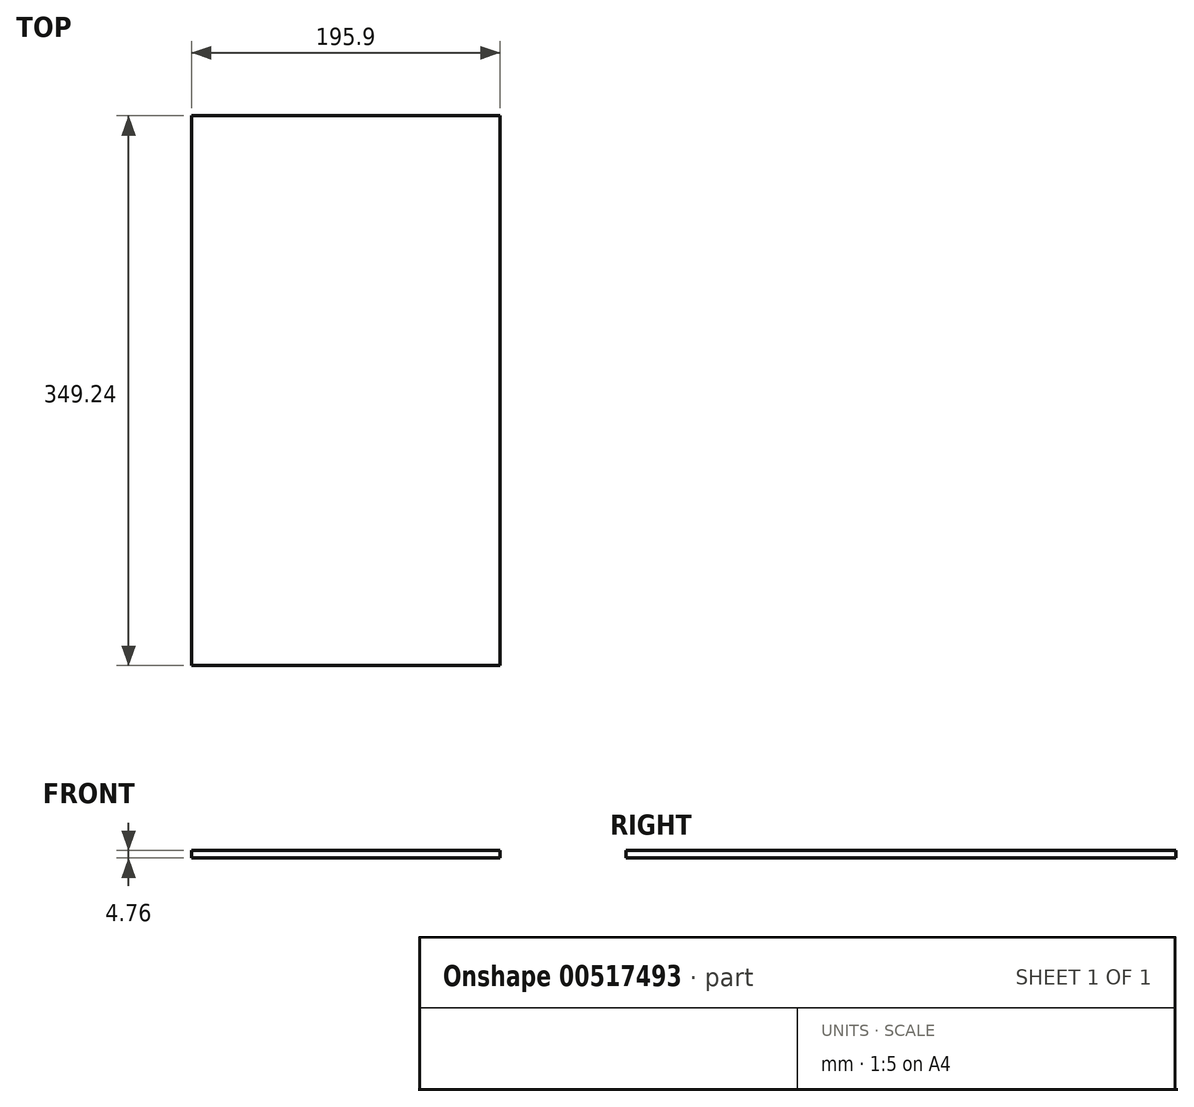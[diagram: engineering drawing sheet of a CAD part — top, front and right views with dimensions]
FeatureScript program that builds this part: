
annotation { "Feature Type Name" : "Feature", "Feature Type Description" : "" }
export const myFeature = defineFeature(function(context is Context, id is Id, definition is map)
    precondition{}
    {
        {
            var Q0;
            Q0=qCreatedBy(makeId("Top.planeOp"),FACE);
            var sketch = newSketch(context, id + "F0", { "sketchPlane" : qUnion([Q0])});
            skLineSegment(sketch, "E0.bottom", {"start": v(97.95, -174.62) * mm, "end": v(-97.95, -174.63) * mm});
            skLineSegment(sketch, "E0.top", {"start": v(97.95, 174.63) * mm, "end": v(-97.95, 174.63) * mm});
            skLineSegment(sketch, "E0.left", {"start": v(97.95, -174.62) * mm, "end": v(97.95, 174.63) * mm});
            skLineSegment(sketch, "E0.right", {"start": v(-97.95, -174.63) * mm, "end": v(-97.95, 174.63) * mm});
            skPoint(sketch, "E0.middle", {"position": v(0, 0) * mm});
            skSolve(sketch);
        }
        {
            var Q0;
            Q0=makeQuery(id+"F0.imprint","IMPRINT",FACE,{"disambiguationData":[TD([[makeQuery(id+"F0.imprint","IMPRINT",EDGE,{"derivedFrom":sQuery(id+"F0.wireOp",EDGE,"E0.bottom")}),-1.0]])]});
            extrude(context, id + "F1", {"entities" : qUnion([Q0]), "depth" : 4.76 * mm, "offsetDistance" : 25.4 * mm});
        }
    });
